# Revit family: 415060001_Lavaplatos 8 In palanca Balta
name_source: partatom
category: Plumbing Fixtures
units: mm (PartAtom-declared; Revit-internal decimal feet)

## family parameters
Cut with Voids When Loaded = No
Host = Face
OmniClass Number = 23.31.11.00
OmniClass Title = Faucets
Part Type = Normal
Room Calculation Point = No
Round Connector Dimension = Use Diameter
Shared = No

## types (1)
- Lavaplatos 8In palanca Balta
    Alto = 319 mm
    Ancho = 327 mm
    Capacidad de flujo = A 60 Psi: 8.3 l/min.
    Ciclo de vida de la unidad de cierre = 500000 ciclos.
    Coatings = Resistente a la corrosión, pelado y decoloración por agua. Recubrimientos no tóxicos. Productos para uso doméstico.}
    Creado por = BIMBAU
    Default Elevation = 0 mm  [stored 0 ft]
    Description = El lavaplatos 8P Balta palanca ha sido diseñada para trabajar en perfecta armonía con el espacio; inspirada en las necesidades del consumidor latinoamericano dando como resultado un producto robusto y funcional. Permite regular la temperatura del agua por medio de dos minjas independientes. Incorpora un sistema aireador que genera un chorro de agua espumoso agradable al tacto.
    Dimensiones generales del producto = 391 x 327 x 236 mm.
    Diámetro abasto = 13 mm  [stored 0.0426509 ft]
    Fecha de creación = 29/04/2021
    Garantía = 30 años Grival - 5 años Cromado.
    Manufacturer = Corona.
    Material = Corona_Plastico_Cromado
    Material 2 = Corona_Plastico_Negro
    Material 3 = Corona_Acero inoxidable
    Model = 415060001_Lavaplatos 8 in palanca Balta
    Normatividad = NTC 1644.
    Peso Bruto aprox = 700 gr. / 1.54 lb.
    Peso Neto aprox = 620 gr. / 1.37 lb.
    Presión máxima recomendada = 125 psi
    Presión mínima recomendada = 20 psi
    Profundidad = 236 mm
    Temperaturas máxima de trabajo = 71° C / 159.8° F.-
    Temperaturas mínima de trabajo = 5°C / 4°F.

note: [stored X ft] marks values corroborated as IEEE doubles in the binary element streams (Revit-internal decimal feet)

## geometry (parser evidence)
native form markers: Sweep x6
no freeform markers — native parametric forms only
